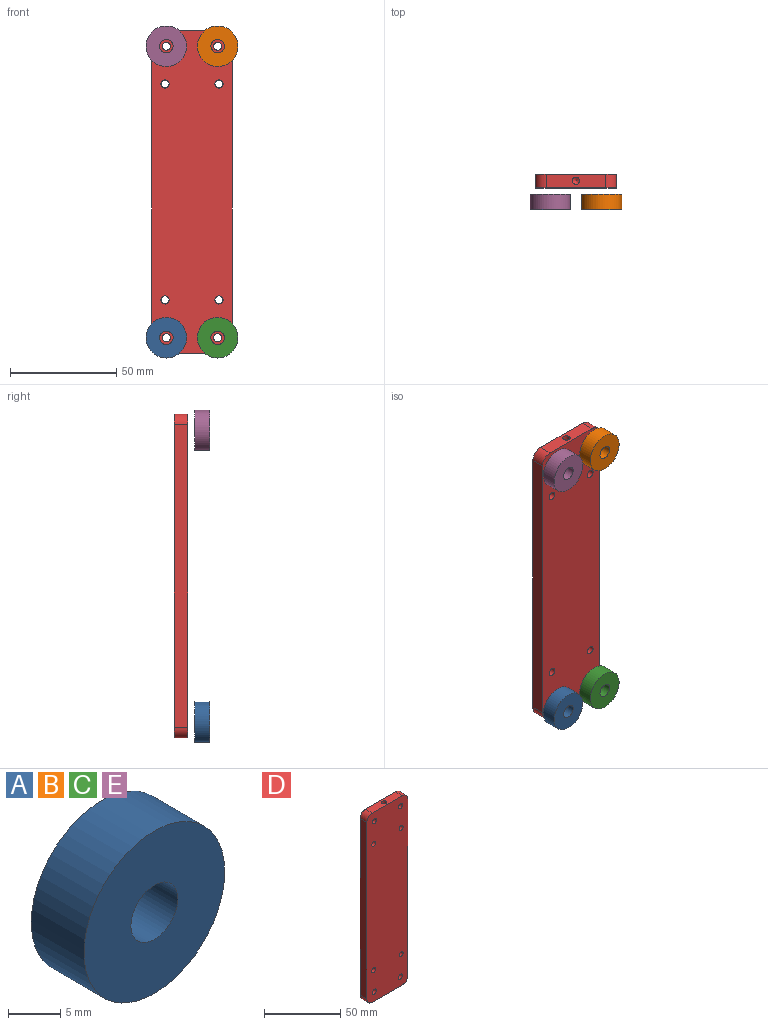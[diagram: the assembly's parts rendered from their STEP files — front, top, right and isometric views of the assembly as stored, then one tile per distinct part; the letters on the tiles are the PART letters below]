
ASSEMBLY  parts=5 mates=4
PART A: 4 faces, bbox 19.1x7.1x19.1 mm
  f0: cylinder r=3.17mm len=7.14mm, axis (0,1,0), area 142.4mm2, adj f2,f3
  f1: cylinder r=9.53mm len=19.05mm, axis (0,1,0), area 427.2mm2, adj f2,f3
  f2: plane 19.05x19.05mm, normal (0,-1,0), area 253.4mm2, adj f0,f1
  f3: plane 19.05x19.05mm, normal (0,1,0), area 253.4mm2, adj f0,f1
PART B: same geometry as A
PART C: same geometry as A
PART D: 22 faces, bbox 38.1x6.4x152.4 mm
  f0: plane 27.94x6.35mm, normal (0,0,1), area 168mm2, adj f12,f13,f14,f15,f19
  f1: plane 142.24x6.35mm, normal (-1,0,0), area 903.2mm2, adj f12,f13,f15,f16
  f2: plane 27.94x6.35mm, normal (0,0,-1), area 168mm2, adj f12,f13,f16,f17,f21
  f3: cylinder r=1.91mm len=6.35mm, axis (0,1,0), area 76mm2, adj f12,f13
  f4: cylinder r=1.91mm len=6.35mm, axis (0,1,0), area 76mm2, adj f12,f13
  f5: cylinder r=1.91mm len=6.35mm, axis (0,1,0), area 76mm2, adj f12,f13
  f6: cylinder r=1.91mm len=6.35mm, axis (0,1,0), area 76mm2, adj f12,f13
  f7: cylinder r=1.91mm len=6.35mm, axis (0,1,0), area 76mm2, adj f12,f13
  f8: cylinder r=1.91mm len=6.35mm, axis (0,1,0), area 76mm2, adj f12,f13
  f9: cylinder r=1.91mm len=6.35mm, axis (0,1,0), area 76mm2, adj f12,f13
  f10: plane 142.24x6.35mm, normal (1,0,0), area 903.2mm2, adj f12,f13,f14,f17
  f11: cylinder r=1.91mm len=6.35mm, axis (0,1,0), area 76mm2, adj f12,f13
  f12: plane 152.4x38.1mm, normal (0,-1,0), area 5693.1mm2, adj f0,f1,f2,f3,f4,f5,f6,f7
  f13: plane 152.4x38.1mm, normal (0,1,0), area 5693.1mm2, adj f0,f1,f2,f3,f4,f5,f6,f7
  f14: cylinder r=5.08mm len=6.35mm, axis (0,1,0), area 50.7mm2, adj f0,f10,f12,f13
  f15: cylinder r=5.08mm len=6.35mm, axis (0,-1,0), area 50.7mm2, adj f0,f1,f12,f13
  f16: cylinder r=5.08mm len=6.35mm, axis (0,1,0), area 50.7mm2, adj f1,f2,f12,f13
  f17: cylinder r=5.08mm len=6.35mm, axis (0,-1,0), area 50.7mm2, adj f2,f10,f12,f13
  f18: cone r=0mm half-angle=59deg, axis (0,0,1), area 10.9mm2, adj f19
  f19: cylinder r=1.73mm len=6.35mm, axis (0,0,1), area 68.9mm2, adj f0,f18
  f20: cone r=0mm half-angle=59deg, axis (0,0,-1), area 10.9mm2, adj f21
  f21: cylinder r=1.73mm len=6.35mm, axis (0,0,-1), area 68.9mm2, adj f2,f20
PART E: same geometry as A
PLACE A t=(-53.01,-16.18,13.14)mm
PLACE B t=(-28.88,-16.18,150.3)mm
PLACE C t=(-28.88,-16.18,13.14)mm
PLACE D t=(-21.89,-6.65,5.52)mm
PLACE E t=(-53.01,-16.18,150.3)mm
MATE fastened C.f0 <-> D.f11  axis (0,1,0) through (-28.88,-16.18,13.14)mm
MATE fastened B.f0 <-> D.f8  axis (0,1,0) through (-28.88,-16.18,150.3)mm
MATE fastened E.f1 <-> D.f7  axis (0,1,0) through (-53.01,-16.18,150.3)mm
MATE fastened A.f1 <-> D.f5  axis (0,1,0) through (-53.01,-16.18,13.14)mm
